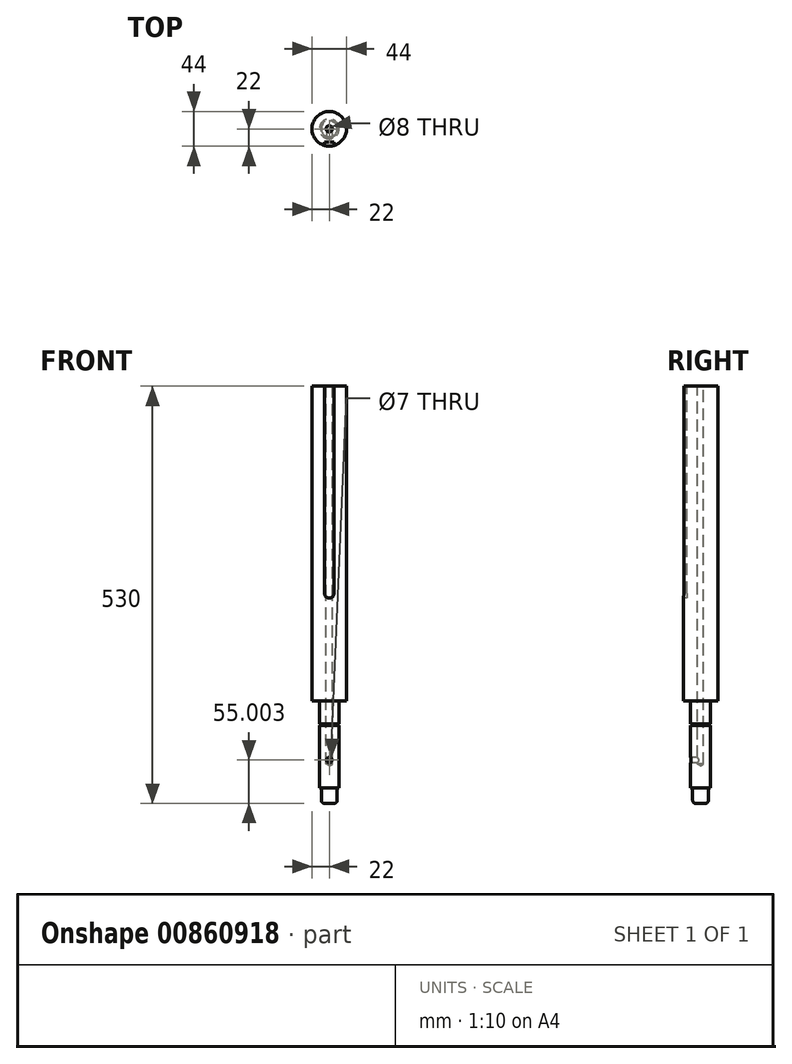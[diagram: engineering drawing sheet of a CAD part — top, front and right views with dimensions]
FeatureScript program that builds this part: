
annotation { "Feature Type Name" : "Feature", "Feature Type Description" : "" }
export const myFeature = defineFeature(function(context is Context, id is Id, definition is map)
    precondition{}
    {
        {
            var Q0;
            Q0=qCreatedBy(makeId("Front.planeOp"),FACE);
            var sketch = newSketch(context, id + "F0", { "sketchPlane" : qUnion([Q0])});
            skLineSegment(sketch, "E0", {"start": v(0, 429.5) * mm, "end": v(0, -164.85) * mm, "construction": true});
            skLineSegment(sketch, "E1", {"start": v(0, 374.54) * mm, "end": v(-22, 374.54) * mm});
            skLineSegment(sketch, "E2", {"start": v(-22, 374.54) * mm, "end": v(-22, -25.46) * mm});
            skLineSegment(sketch, "E3", {"start": v(-12.5, -27.46) * mm, "end": v(-12.5, -54.46) * mm});
            skLineSegment(sketch, "E4", {"start": v(-10, -155.46) * mm, "end": v(0, -155.46) * mm});
            skLineSegment(sketch, "E5", {"start": v(0, 374.54) * mm, "end": v(0, -155.46) * mm});
            skLineSegment(sketch, "E6", {"start": v(-22, -25.46) * mm, "end": v(-14.5, -25.46) * mm});
            skLineSegment(sketch, "E7", {"start": v(-12.5, -135.46) * mm, "end": v(-12, -135.46) * mm});
            skLineSegment(sketch, "E8", {"start": v(-10, -137.46) * mm, "end": v(-10, -155.46) * mm});
            skPoint(sketch, "E9.visualSharp", {"position": v(-12.5, -25.46) * mm});
            skArc(sketch, "E9.filletArc", {"start": v(-12.5, -27.46) * mm, "mid": v(-13.09, -26.04) * mm, "end": v(-14.5, -25.46) * mm});
            skPoint(sketch, "E10.visualSharp", {"position": v(-10, -135.46) * mm});
            skArc(sketch, "E10.filletArc", {"start": v(-10, -137.46) * mm, "mid": v(-10.59, -136.04) * mm, "end": v(-12, -135.46) * mm});
            skLineSegment(sketch, "E11", {"start": v(-12.5, -54.46) * mm, "end": v(-11, -54.46) * mm});
            skLineSegment(sketch, "E12", {"start": v(-11, -54.46) * mm, "end": v(-11, -56.46) * mm});
            skLineSegment(sketch, "E13", {"start": v(-11, -56.46) * mm, "end": v(-12.5, -56.46) * mm});
            skLineSegment(sketch, "E14.trimOffspring", {"start": v(-12.5, -56.46) * mm, "end": v(-12.5, -135.46) * mm});
            skSolve(sketch);
        }
        {
            var Q0;
            Q0 = qSketchRegion(id + "F0", true);
            var Q1;
            Q1=sQuery(id+"F0.wireOp",EDGE,"E0");
            revolve(context, id + "F1", {"surfaceOperationType" : NewSurfaceOperationType.NEW, "entities" : qUnion([Q0]), "axis" : qUnion([Q1]), "revolveType" : RevolveType.FULL});
        }
        {
            var Q0;
            Q0=makeQuery(id+"F1.opRevolve","SWEPT_FACE",FACE,{"disambiguationData":[OSD([sQuery(id+"F0.wireOp",EDGE,"E1")])]});
            var sketch = newSketch(context, id + "F2", { "sketchPlane" : qUnion([Q0])});
            skCircle(sketch, "E15", {"center": v(0, 0) * mm, "radius": 4 * mm});
            skSolve(sketch);
        }
        {
            var Q0;
            Q0=qCreatedBy(makeId("Front.planeOp"),FACE);
            cPlane(context, id + "F3", {"entities" : qUnion([Q0]), "cplaneType" : CPlaneType.OFFSET, "offset" : 22 * mm, "width" : 150 * mm, "height" : 150 * mm});
        }
        {
            var Q0;
            Q0=qCreatedBy(id+"F3.planeOp",FACE);
            var sketch = newSketch(context, id + "F4", { "sketchPlane" : qUnion([Q0])});
            skLineSegment(sketch, "E16.top", {"start": v(6, 643.54) * mm, "end": v(-6, 643.54) * mm});
            skLineSegment(sketch, "E16.left", {"start": v(6, 111.54) * mm, "end": v(6, 643.54) * mm});
            skLineSegment(sketch, "E16.right", {"start": v(-6, 111.54) * mm, "end": v(-6, 643.54) * mm});
            skPoint(sketch, "E16.middle", {"position": v(0, 374.54) * mm});
            skArc(sketch, "E17", {"start": v(-6, 111.54) * mm, "mid": v(0, 105.54) * mm, "end": v(6, 111.54) * mm});
            skPoint(sketch, "E18", {"position": v(0, 105.54) * mm});
            skPoint(sketch, "E19.orphan", {"position": v(-6, 105.54) * mm});
            skPoint(sketch, "E20.orphan", {"position": v(6, 105.54) * mm});
            skSolve(sketch);
        }
        {
            var Q0;
            Q0 = qSketchRegion(id + "F4", true);
            extrude(context, id + "F5", {"entities" : qUnion([Q0]), "operationType" : NewBodyOperationType.REMOVE, "oppositeDirection" : true, "depth" : 5 * mm, "offsetDistance" : 25 * mm});
        }
        {
            var Q0;
            Q0=makeQuery(id+"F1.opRevolve","SWEPT_EDGE",EDGE,{"disambiguationData":[OSD([sQuery(id+"F0.wireOp",EDGE,"E4"),sQuery(id+"F0.wireOp",EDGE,"E8")])]});
            fillet(context, id + "F6", {"entities" : qUnion([Q0]), "radius" : 4 * mm, "tangentPropagation" : true, "allowEdgeOverflow" : false});
        }
        {
            var Q0;
            Q0=qCreatedBy(id+"F3.planeOp",FACE);
            var sketch = newSketch(context, id + "F7", { "sketchPlane" : qUnion([Q0])});
            skCircle(sketch, "E21", {"center": v(0, -100.46) * mm, "radius": 3.5 * mm});
            skSolve(sketch);
        }
        {
            var Q0;
            Q0 = qSketchRegion(id + "F7", true);
            extrude(context, id + "F8", {"entities" : qUnion([Q0]), "operationType" : NewBodyOperationType.REMOVE, "oppositeDirection" : true, "depth" : 22 * mm, "offsetDistance" : 25 * mm});
        }
        {
            var Q0;
            Q0=makeQuery(id+"F1.opRevolve","SWEPT_FACE",FACE,{"disambiguationData":[OSD([sQuery(id+"F0.wireOp",EDGE,"E1")])]});
            var sketch = newSketch(context, id + "F9", { "sketchPlane" : qUnion([Q0])});
            skPoint(sketch, "E22", {"position": v(0, 0) * mm});
            skSolve(sketch);
        }
        {
            var Q0;
            Q0=sQuery(id+"F9.wireOp",VERTEX,"E22");
            var Q1;
            Q1=makeQuery(id+"F1.opRevolve","SWEPT_BODY",BODY,{"disambiguationData":[OSD([sQuery(id+"F0.wireOp",EDGE,"E1"),sQuery(id+"F0.wireOp",EDGE,"E2"),sQuery(id+"F0.wireOp",EDGE,"E3"),sQuery(id+"F0.wireOp",EDGE,"E4"),sQuery(id+"F0.wireOp",EDGE,"E5"),sQuery(id+"F0.wireOp",EDGE,"E6"),sQuery(id+"F0.wireOp",EDGE,"E7"),sQuery(id+"F0.wireOp",EDGE,"E8"),sQuery(id+"F0.wireOp",EDGE,"E9.filletArc"),sQuery(id+"F0.wireOp",EDGE,"E10.filletArc"),sQuery(id+"F0.wireOp",EDGE,"E11"),sQuery(id+"F0.wireOp",EDGE,"E12"),sQuery(id+"F0.wireOp",EDGE,"E13"),sQuery(id+"F0.wireOp",EDGE,"E14.trimOffspring")])]});
            hole(context, id + "F10", {"style" : HoleStyle.SIMPLE, "endStyle" : HoleEndStyle.BLIND, "standardTappedOrClearance" : lookupTablePath({ "standard" : "ISO", "size" : "8", "type" : "Drilled" }), "standardBlindInLast" : lookupTablePath({ "standard" : "ISO", "size" : "8", "type" : "Drilled" }), "holeDiameter" : 8 * mm, "majorDiameter" : 5 * mm, "holeDepth" : 480 * mm, "isTappedThrough" : true, "tappedDepth" : 27.9 * mm, "tapClearance" : 3, "startFromSketch" : true, "locations" : qUnion([Q0]), "scope" : qUnion([Q1])});
        }
    });
